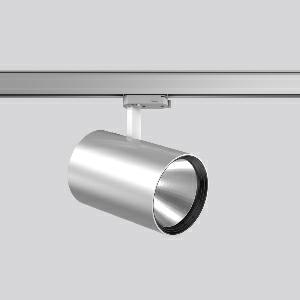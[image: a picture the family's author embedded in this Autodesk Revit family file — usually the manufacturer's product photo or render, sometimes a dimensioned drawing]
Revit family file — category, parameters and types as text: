
# Revit family: deecos_s_maxi_742213_004_3_9cea
name_source: partatom
category: Lighting Fixtures
units: mm (PartAtom-declared; Revit-internal decimal feet)

## family parameters
Cut with Voids When Loaded = No
Host = Face
Light Source = No
Part Type = Normal
Room Calculation Point = No
Round Connector Dimension = Use Diameter
Shared = No

## types (1)
- DEECOS S maxi (1 x LED Modul 935, 3300 lm, 3500)
    Apparent Load = 25 VA
    Approval mark = CE
    CIE Flux Codes = 100 100 100 100 100
    Color Rendering = 92
    Color Temperature = 3500
    Default Elevation = 1800 mm
    Description = Series: DEECOS S maxi
LED surface-mounted projector in modern design with no visible cooling ribs. Housing: die-cast aluminium, powder-coated. Rotation range: 356°. Swivel range: 90°. Black plastic ring and recessed LED to prevent glare from the side. Optical assembly with reflector made of MIRO-Silver with 98% total light reflection for outstanding efficiency - can be changed without tools. Best colour rendering index Ra>90. With multi adaptor for 3-circuit tracks 230 V. Suitable for Track on ceiling, Wall track. High quality converter without flickering and stroboscopic effect. The following accessories can be mounted without use of tools: interchangeable lenses, decorative glasses, honeycomb louvre, clear and frosted diffusers, white interchangeable plastic ring. 
Colour: silver
Diameter: 123 mm
Height: 200 mm
Lamp: LED
Socket: without socket
Colour temperature: 3500K
Colour rendering index (CRI): 92
System power: 25 W
Rated luminous flux: 3300 lm
Luminous efficiency: 132 lm/W
Control gear: Regulated power supply
Protection class: I
Type of protection: IP 20
    Height = 200 mm
    Lamp = 1 x LED Modul 935
    Lamp Light Flux = 3300 lm
    Lamp count = 1
    Length = 123 mm
    Lifetime = 50000 h
    Luminous efficacy = 132 lm/W
    Manufacturer = RZB
    ModVariant = No
    Model = 742213.004.3
    Mounting Place = Ceiling
    Mounting Type = Rail mounted
    Number of Poles = 1
    OnlyDefault = Yes
    Power Factor = 1
    Product Name = DEECOS S maxi
    Product group = Track mounted projectors
    ProductGroupID = 301
    Protection Class = Protection class I
    Protection Degree = IP 20
    RLX_Detail_Level = 1
    RLX_Emergency_Light_Flux = 0 lm
    RLX_Emergency_Type = 0
    RLX_Emergency_Type_DB = No
    RlxData = <blob elided: 40541 chars, md5=72c55112>
    Socket = socket
    Standby Power = 0 W
    System Light Flux = 3300 lm
    System Power = 25 W
    Type Comments = Product without accessories
    Type Image = 741954.004.jpg
    URL = http://relux.com
    VarID = ---
    Voltage = 230 V
    Voltage Range = 220-240 V
    Weight = 0.00 kg
    Width = 0 mm  [stored 0 ft]

note: [stored X ft] marks values corroborated as IEEE doubles in the binary element streams (Revit-internal decimal feet)

## geometry (parser evidence)
native form markers: Blend x4, Sweep x10
no freeform markers — native parametric forms only
